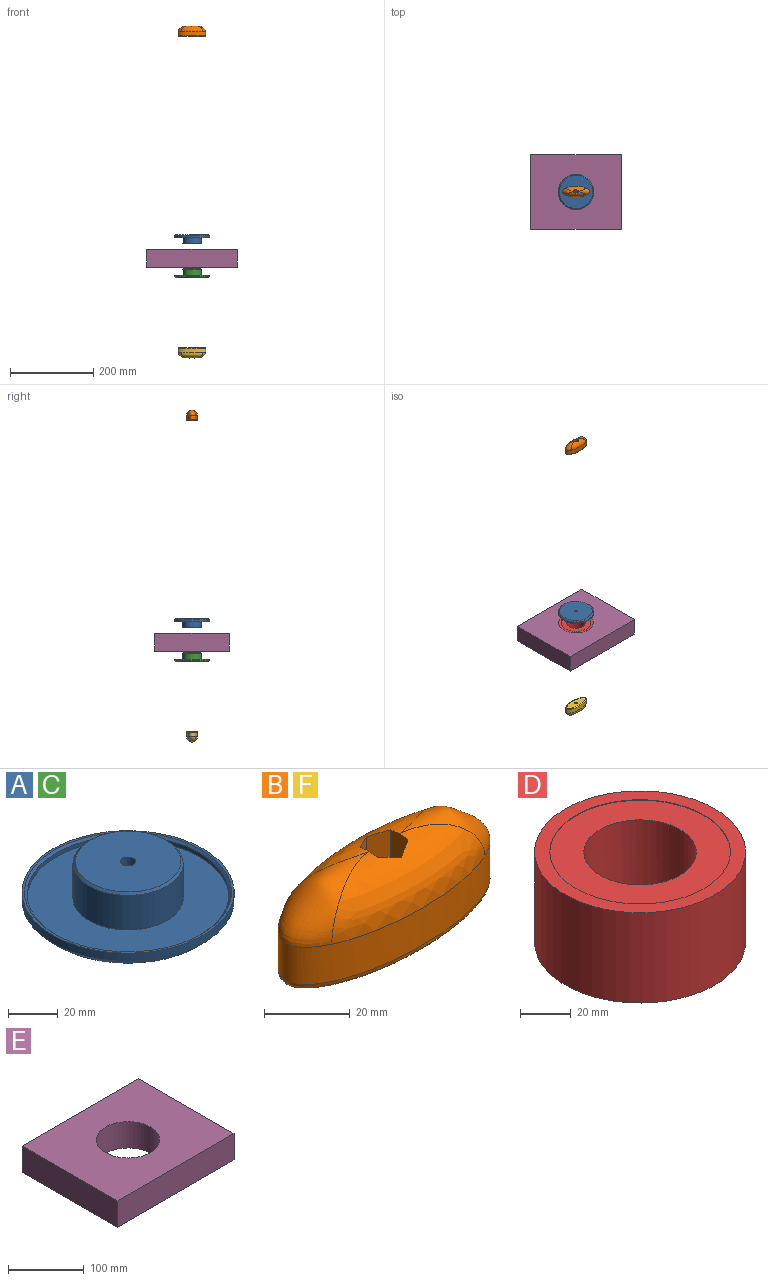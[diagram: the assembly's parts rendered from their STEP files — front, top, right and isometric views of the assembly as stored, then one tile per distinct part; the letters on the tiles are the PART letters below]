
ASSEMBLY  parts=6 mates=5
PART A: 11 faces, bbox 85.1x85.1x22 mm
  f0: cylinder r=42.55mm len=85.1mm, axis (0,0,-1), area 1069.4mm2, adj f1,f10
  f1: plane 85.1x85.1mm, normal (0,0,1), area 264.2mm2, adj f0,f8
  f2: plane 79.1x79.1mm, normal (0,0,-1), area 4884.9mm2, adj f7,f10
  f3: cylinder r=40.55mm len=81.1mm, axis (0,0,1), area 509.6mm2, adj f4,f8
  f4: plane 81.1x81.1mm, normal (0,0,1), area 3624.4mm2, adj f3,f5
  f5: cylinder r=22.15mm len=44.3mm, axis (0,0,-1), area 2365.9mm2, adj f4,f9
  f6: plane 42.3x42.3mm, normal (0,0,1), area 1376.1mm2, adj f7,f9
  f7: cylinder r=3.05mm len=22mm, axis (0,0,-1), area 421.6mm2, adj f2,f6
  f8: cone r=40.55mm half-angle=45deg, axis (0,0,1), area 364.8mm2, adj f1,f3
  f9: cone r=21.15mm half-angle=45deg, axis (0,0,-1), area 192.4mm2, adj f5,f6
  f10: cone r=42.55mm half-angle=45deg, axis (0,0,1), area 1094.3mm2, adj f0,f2
PART B: 17 faces, bbox 65.2x25.4x25.2 mm
  f0: plane 0.42x0.06mm, normal (0,0,1), area 0mm2, adj f4,f13,f14
  f1: plane 0.42x0.06mm, normal (0,0,1), area 0mm2, adj f7,f13,f14
  f2: extruded ~65.03x25.21mm, area 1577.1mm2, adj f12,f13,f14,f15,f16
  f3: plane 61.05x21.22mm, normal (0,0,-1), area 973.8mm2, adj f11,f16
  f4: plane 15.07x5.84mm, normal (-1,0,0), area 86mm2, adj f0,f5,f9,f10,f13,f14
  f5: plane 14.83x5.17mm, normal (-0.5,-0.87,0), area 82.2mm2, adj f4,f6,f10,f13
  f6: plane 14.82x5.15mm, normal (0.5,-0.87,0), area 82.2mm2, adj f5,f7,f10,f13
  f7: plane 15.07x5.84mm, normal (1,0,0), area 86mm2, adj f1,f6,f8,f10,f13,f14
  f8: plane 14.83x5.17mm, normal (0.5,0.87,0), area 82.2mm2, adj f7,f9,f10,f14
  f9: plane 14.82x5.15mm, normal (-0.5,0.87,0), area 82.2mm2, adj f4,f8,f10,f14
  f10: plane 11.55x10mm, normal (0,0,1), area 57.4mm2, adj f4,f5,f6,f7,f8,f9,f11
  f11: cylinder r=3.05mm len=10mm, axis (0,0,-1), area 191.6mm2, adj f3,f10
  f12: bspline ~27.1x15.98mm, area 257mm2, adj f2,f13,f14
  f13: bspline ~51.55x16.02mm, area 716.3mm2, adj f0,f1,f2,f4,f5,f6,f7,f12
  f14: bspline ~51.73x16.04mm, area 717.1mm2, adj f0,f1,f2,f4,f7,f8,f9,f12
  f15: bspline ~27.1x15.96mm, area 256.7mm2, adj f2,f13,f14
  f16: bspline ~65.05x25.23mm, area 453.5mm2, adj f2,f3
PART C: same geometry as A
PART D: 8 faces, bbox 83.1x83.1x43.5 mm
  f0: cylinder r=22.15mm len=44.3mm, axis (0,0,1), area 5984.4mm2, adj f5,f6
  f1: cylinder r=41.55mm len=83.1mm, axis (0,0,-1), area 11356.4mm2, adj f2,f3
  f2: plane 83.1x83.1mm, normal (0,0,1), area 1453.3mm2, adj f1,f4
  f3: plane 83.1x83.1mm, normal (0,0,-1), area 1083.2mm2, adj f1,f7
  f4: cylinder r=35.55mm len=71.1mm, axis (0,0,1), area 55.8mm2, adj f2,f5
  f5: plane 71.1x71.1mm, normal (0,0,1), area 2429mm2, adj f0,f4
  f6: plane 74.34x74.34mm, normal (0,0,-1), area 2799.1mm2, adj f0,f7
  f7: cylinder r=37.17mm len=74.34mm, axis (0,0,-1), area 58.4mm2, adj f3,f6
PART E: 7 faces, bbox 217.7x177.7x42.5 mm
  f0: plane 177.68x42.5mm, normal (1,0,0), area 7551.2mm2, adj f1,f3,f4,f5
  f1: plane 217.66x42.5mm, normal (0,1,0), area 9250.5mm2, adj f0,f2,f4,f5
  f2: plane 177.68x42.5mm, normal (-1,0,0), area 7551.2mm2, adj f1,f3,f4,f5
  f3: plane 217.66x42.5mm, normal (0,-1,0), area 9250.5mm2, adj f0,f2,f4,f5
  f4: plane 217.66x177.68mm, normal (0,0,1), area 33249mm2, adj f0,f1,f2,f3,f6
  f5: plane 217.66x177.68mm, normal (0,0,-1), area 33249mm2, adj f0,f1,f2,f3,f6
  f6: cylinder r=41.55mm len=83.1mm, axis (0,0,1), area 11095.3mm2, adj f4,f5
PART F: same geometry as B
PLACE A rot(axis=(1,0,0),180deg) t=(-10.09,15.93,60.68)mm
PLACE B t=(-10.09,15.93,535.67)mm
PLACE C t=(-10.09,15.93,-42.97)mm
PLACE D rot(axis=(0,0,-1),0deg) t=(-10.09,15.93,-18.04)mm
PLACE E t=(-10.09,15.93,-17.35)mm
PLACE F rot(axis=(1,0,0),180deg) t=(-10.09,15.93,-209.83)mm
MATE cylindrical D.f0 <-> C.f5  axis (0,0,1) through (-10.09,15.93,-17.79)mm
MATE cylindrical D.f1 <-> E.f6  axis (0,0,-1) through (-10.09,15.93,3.71)mm
MATE cylindrical A.f5 <-> D.f0  axis (0,0,1) through (-10.09,15.93,39.68)mm
MATE cylindrical A.f7 <-> B.f11  axis (0,0,1) through (-10.09,15.93,49.68)mm
MATE cylindrical C.f7 <-> F.f11  axis (0,0,-1) through (-10.09,15.93,-31.97)mm
